# Revit family: IS_TonicII_K5238_BIM_DE
name_source: partatom
category: Plumbing Fixtures
revit_build: Autodesk Revit MEP 2016 (Build: 20161004_0715(x64)
units: mm (PartAtom-declared; Revit-internal decimal feet)

## family parameters
Cut with Voids When Loaded = No
Host = Face
OmniClass Number = 23.45.05.14.14.14
OmniClass Title = Clinic Sinks
Part Type = Normal
Room Calculation Point = No
Round Connector Dimension = Use Diameter
Shared = Yes

## types (1)
- K523801 - TONIC II BTW BID  WHITE 1TH & OF
    Accessories = www.idealstandard.de\ersatzteile
    AreaUnits = millimeters
    Assembly Code = C1030200
    AssetType = Fixed
    BIMObjectName = ISI_IdealStandard_Washbasins_TONIC II_K523801
    BarCode = 4015413061605
    Brand = Ideal Standard
    CWFU = 0
    CodePerformance = 0
    Color = White
    ConnectionType = Plumbing
    Cost = 0 $
    CurrencyUnit = €
    Default Elevation = 0 mm  [stored 0 ft]
    Description = Tonic ii btw bid  white 1th & of
    DurationUnit = year
    ExpectedLife = 25
    Features = TONIC II floor standing bidet 355x560mm, 1 taphole
    Finish = White
    GrossWeight = 24,9 kg
    HWFU = 0
    InstallationDate = 1900-12-31T23:59:59
    InstallationInstructions = www.idealstandard.de\produkte
    LinearUnits = millimeters
    ManufacturerURL = www.idealstandard.de
    Material = Vitreous china
    MetalFinish = ASH_ArmitageShanks_StainlessSteel_Silver_Render
    Model = K523801
    ModelNumber = K523801
    ModelReference = IS Standbidet TONIC II, 1Hl., 355x560x400mm, Weiß
    Name = ISI_IdealStandard_Washbasins_TONIC II_K523801
    NominalDepth = 0 mm  [stored 0 ft]
    NominalHeight = 400 mm
    NominalLength = 560 mm
    NominalWidth = 355 mm
    ProductInformation = www.idealstandard.de
    Shape = Sculptured
    Size = 560 x 355 x 400 mm
    Space = Internal
    URL = www.idealstandard.de
    Uniclass2015Code = Pr_40_20_06_11
    Uniclass2015Title = Bidets
    Uniclass2015Version = Products v1.1
    Version = 1
    VolumeUnits = Litres
    WFU = 0

note: [stored X ft] marks values corroborated as IEEE doubles in the binary element streams (Revit-internal decimal feet)

## geometry (parser evidence)
native form markers: Blend x6, Sweep x1
no freeform markers — native parametric forms only
